FCSTD DOCUMENT  (FreeCAD 0.21R32532 (Git))
Label: 24
License: All rights reserved
LicenseURL: http://en.wikipedia.org/wiki/All_rights_reserved
objects: Part::Feature×2, Part::FeaturePython×1, Sketcher::SketchObject×1, App::ImagePlane×1
note: 4 computed .brp shape members not serialized (recipe doc carries the construction recipe); baked Part::Feature solids carry a one-line shape summary decoded from their .brp

FEATURE [Part::Feature] LAYER_0
  shape: bbox 2565 x 3338 x 2e-07 mm, 0 faces, 0 solids (baked)
FEATURE [Part::Feature] UNFOLD_SKETCH004
  shape: bbox 2221 x 2866 x 2e-07 mm, 0 faces, 0 solids (baked)
FEATURE [Part::FeaturePython] Clone  label="LAYER_001"  # Draft clone (typed FeaturePython)
  AttacherType = Attacher::AttachEngine3D
  Fuse = false
  Objects = -> [LAYER_0,UNFOLD_SKETCH004]
  Scale = (0.0393701,0.0393701,0.0393701)
  expr: Scale = tuple(1 / 25.4; 1 / 25.4; 1 / 25.4)
FEATURE [Sketcher::SketchObject] Sketch
  FullyConstrained = false
  sketch-geometry (18):
    g0: LineSegment StartX=-50.5 StartY=-25 StartZ=0 EndX=50.5 EndY=-25 EndZ=0
    g1: LineSegment StartX=50.5 StartY=-25 StartZ=0 EndX=50.5 EndY=0.382 EndZ=0
    g2: LineSegment StartX=46.9279 StartY=8.04244 StartZ=0 EndX=-15.0274 EndY=60.0291 EndZ=0
    g3: LineSegment StartX=-37.9839 StartY=106.398 StartZ=0 EndX=-48 EndY=106.398 EndZ=0
    g4: LineSegment StartX=-50.5 StartY=103.898 StartZ=0 EndX=-50.5 EndY=-25 EndZ=0
    g5: Circle CenterX=-43 CenterY=10.3982 CenterZ=0 NormalX=0 NormalY=0 NormalZ=1 AngleXU=0 Radius=1.7
    g6: Circle CenterX=-43 CenterY=39.0649 CenterZ=0 NormalX=0 NormalY=0 NormalZ=1 AngleXU=0 Radius=1.7
    g7: Circle CenterX=-43 CenterY=67.7316 CenterZ=0 NormalX=0 NormalY=0 NormalZ=1 AngleXU=0 Radius=1.7
    g8: Circle CenterX=-43 CenterY=96.3982 CenterZ=0 NormalX=0 NormalY=0 NormalZ=1 AngleXU=0 Radius=1.7
    g9: Circle CenterX=-40 CenterY=-12 CenterZ=0 NormalX=0 NormalY=0 NormalZ=1 AngleXU=0 Radius=2.75
    g10: Circle CenterX=40 CenterY=-12 CenterZ=0 NormalX=0 NormalY=0 NormalZ=1 AngleXU=0 Radius=2.75
    g11: ArcOfCircle CenterX=21.7831 CenterY=103.898 CenterZ=0 NormalX=0 NormalY=0 NormalZ=1 AngleXU=0 Radius=57.267 StartAngle=3.14159 EndAngle=4.01426
    g12: ArcOfCircle CenterX=40.5 CenterY=0.382 CenterZ=0 NormalX=0 NormalY=0 NormalZ=1 AngleXU=0 Radius=10 StartAngle=0 EndAngle=0.872665
    g13: GeomPoint X=50.5 Y=5.04508 Z=0
    g14: ArcOfCircle CenterX=-37.9839 CenterY=103.898 CenterZ=0 NormalX=0 NormalY=0 NormalZ=1 AngleXU=0 Radius=2.5 StartAngle=-1.8e-15 EndAngle=1.5708
    g15: LineSegment StartX=-35.4839 StartY=103.898 StartZ=0 EndX=-35.4839 EndY=112.841 EndZ=0
    g16: ArcOfCircle CenterX=-48 CenterY=103.898 CenterZ=0 NormalX=0 NormalY=0 NormalZ=1 AngleXU=0 Radius=2.5 StartAngle=1.5708 EndAngle=3.14159
    g17: GeomPoint X=-50.5 Y=106.398 Z=0
  constraints (40):
    c: Coincident(g0,g1)
    c: Vertical(g1)
    c: Horizontal(g3)
    c: Coincident(g4,g0)
    c: Vertical(g4)
    c: Symmetric(g0,g0,g-2)
    c: DistanceY(g0) = -25
    c: DistanceX(g0,g0) = 101
    c: Equal(g10,g9)
    c: Equal(g5,g6)
    c: Equal(g6,g7)
    c: Equal(g7,g8)
    c: Block(g9)
    c: Block(g10)
    c: Block(g5)
    c: Block(g6)
    c: Block(g7)
    c: Block(g8)
    c: Diameter(g10) = 5.5
    c: Diameter(g5) = 3.4
    c: DistanceY(g8,g17) = 10
    c: Angle(g2) = 2.44346
    c: Tangent(g2,g11) = 1.5708
    c: PointOnObject(g13,g1)
    c: PointOnObject(g13,g2)
    c: Tangent(g1,g12) = -1.5708
    c: Tangent(g2,g12) = -1.5708
    c: Radius(g12) = 10
    c: DistanceY(g12) = 0.382
    c: Tangent(g14,g3) = -1.5708
    c: Tangent(g14,g11) = 1.5708
    c: Vertical(g15)
    c: Tangent(g15,g11) = 1.5708
    c: Diameter(g14) = 5
    c: PointOnObject(g17,g3)
    c: PointOnObject(g17,g4)
    c: Tangent(g3,g16) = -1.5708
    c: Tangent(g4,g16) = -1.5708
    c: Equal(g16,g14)
    c: Radius(g11) = 57.267
FEATURE [App::ImagePlane] pillar_bottom
  XSize = 157.407
  YSize = 222.751
